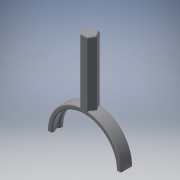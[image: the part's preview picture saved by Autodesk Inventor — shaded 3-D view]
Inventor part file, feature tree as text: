
AUTODESK INVENTOR PART (.ipt)
format: ipt  version: 2016 (Build 200138000, 138)  size: 225,792 bytes
history: native  units: mm
features: fillet x4, extrude x3, sketch x3, plane x2, revolve x1
ambient origin geometry x8: Origin, YZ Plane, XZ Plane, XY Plane, X Axis, Y Axis, Z Axis, Center Point
bodies: Solid1 (feature_tree)
feature tree (13):
  revolve  "Revolution1"  [1 undecoded]
  plane  "Work Plane1"
  extrude  "Extrusion1"  Depth=7.0mm
  fillet  "Fillet2"  Radius=5.0mm
  fillet  "Fillet4"  [1 undecoded]
  fillet  "Fillet5"  Radius=50.0mm
  plane  "Work Plane2"
  extrude  "Extrusion2"  Depth=2.0mm
  extrude  "Extrusion3"  Depth=2.0mm
  fillet  "Fillet8"  Radius=1.0mm
  sketch  "Sketch1"  dims[d0=50.0mm d1=9.0mm]
  sketch  "Sketch3"  dims[d2=5.0mm d3=7.0mm d4=5.0mm d5=90.0deg d6=50.0mm]
  sketch  "Sketch4"  dims[d8=100.0mm d9=0.0mm d11=2.0mm d13=2.0mm d14=1.0mm d15=0.0mm d16=20.0mm d17=0.0mm d18=1.984375mm d19=3.5mm d20=3.5mm d21=6.985mm d22=0.0mm d23=18.0mm d26=2.0mm]
note: 2 required parameter values undecoded (feature->parameter linkage not recoverable at this tier; creation-order binding heuristic only, values carry confidence <= 0.55)